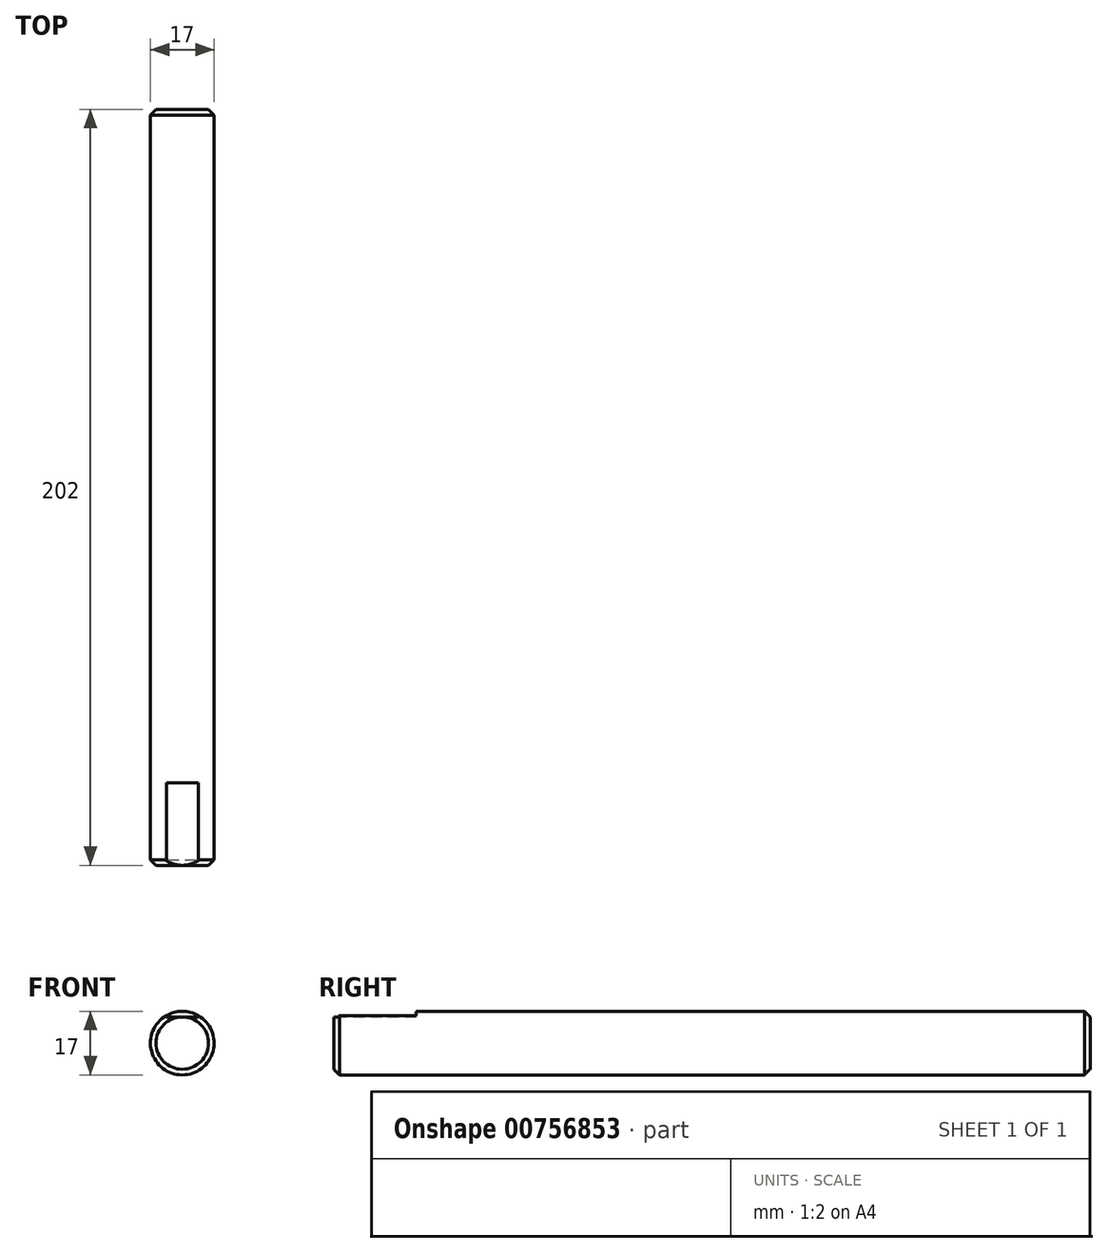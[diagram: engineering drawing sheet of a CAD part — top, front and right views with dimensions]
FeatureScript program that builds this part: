
annotation { "Feature Type Name" : "Feature", "Feature Type Description" : "" }
export const myFeature = defineFeature(function(context is Context, id is Id, definition is map)
    precondition{}
    {
        {
            var Q0;
            Q0=qCreatedBy(makeId("Front.planeOp"),FACE);
            var sketch = newSketch(context, id + "F0", { "sketchPlane" : qUnion([Q0])});
            skCircle(sketch, "E0", {"center": v(0, 0) * mm, "radius": 8.5 * mm});
            skSolve(sketch);
        }
        {
            var Q0;
            Q0=makeQuery(id+"F0.imprint","IMPRINT",FACE,{"disambiguationData":[TD([[makeQuery(id+"F0.imprint","IMPRINT",EDGE,{"derivedFrom":sQuery(id+"F0.wireOp",EDGE,"E0")}),1.0]])]});
            extrude(context, id + "F1", {"entities" : qUnion([Q0]), "depth" : 101 * mm, "offsetDistance" : 25 * mm, "hasSecondDirection" : true, "secondDirectionOppositeDirection" : true, "secondDirectionDepth" : 101 * mm});
        }
        {
            var Q0;
            Q0=makeQuery(id+"F1.opExtrude","CAP_EDGE",EDGE,{"disambiguationData":[OSD([sQuery(id+"F0.wireOp",EDGE,"E0")])],"isStart":false});
            var Q1;
            Q1=makeQuery(id+"F1.opExtrude","CAP_EDGE",EDGE,{"disambiguationData":[OSD([sQuery(id+"F0.wireOp",EDGE,"E0")])],"isStart":true});
            chamfer(context, id + "F2", {"entities" : qUnion([Q0, Q1]), "width" : 1.5 * mm, "tangentPropagation" : true});
        }
        {
            var Q0;
            Q0=qCreatedBy(makeId("Top.planeOp"),FACE);
            cPlane(context, id + "F3", {"entities" : qUnion([Q0]), "cplaneType" : CPlaneType.OFFSET, "offset" : 8.5 * mm, "width" : 150 * mm, "height" : 150 * mm});
        }
        {
            var Q0;
            Q0=qCreatedBy(id+"F3.planeOp",FACE);
            var sketch = newSketch(context, id + "F4", { "sketchPlane" : qUnion([Q0])});
            skLineSegment(sketch, "E1.bottom", {"start": v(-4.25, -79) * mm, "end": v(4.25, -79) * mm});
            skLineSegment(sketch, "E1.top", {"start": v(-4.25, -101) * mm, "end": v(4.25, -101) * mm});
            skLineSegment(sketch, "E1.left", {"start": v(-4.25, -79) * mm, "end": v(-4.25, -101) * mm});
            skLineSegment(sketch, "E1.right", {"start": v(4.25, -79) * mm, "end": v(4.25, -101) * mm});
            skLineSegment(sketch, "E2.0", {"start": v(7, -101) * mm, "end": v(-7, -101) * mm});
            skSolve(sketch);
        }
        {
            var Q0;
            Q0=makeQuery(id+"F4.imprint","IMPRINT",FACE,{"disambiguationData":[TD([[makeQuery(id+"F4.imprint","IMPRINT",EDGE,{"derivedFrom":sQuery(id+"F4.wireOp",EDGE,"E1.bottom")}),-1.0]])]});
            extrude(context, id + "F5", {"entities" : qUnion([Q0]), "operationType" : NewBodyOperationType.REMOVE, "oppositeDirection" : true, "depth" : 1.5 * mm, "offsetDistance" : 25 * mm});
        }
    });
